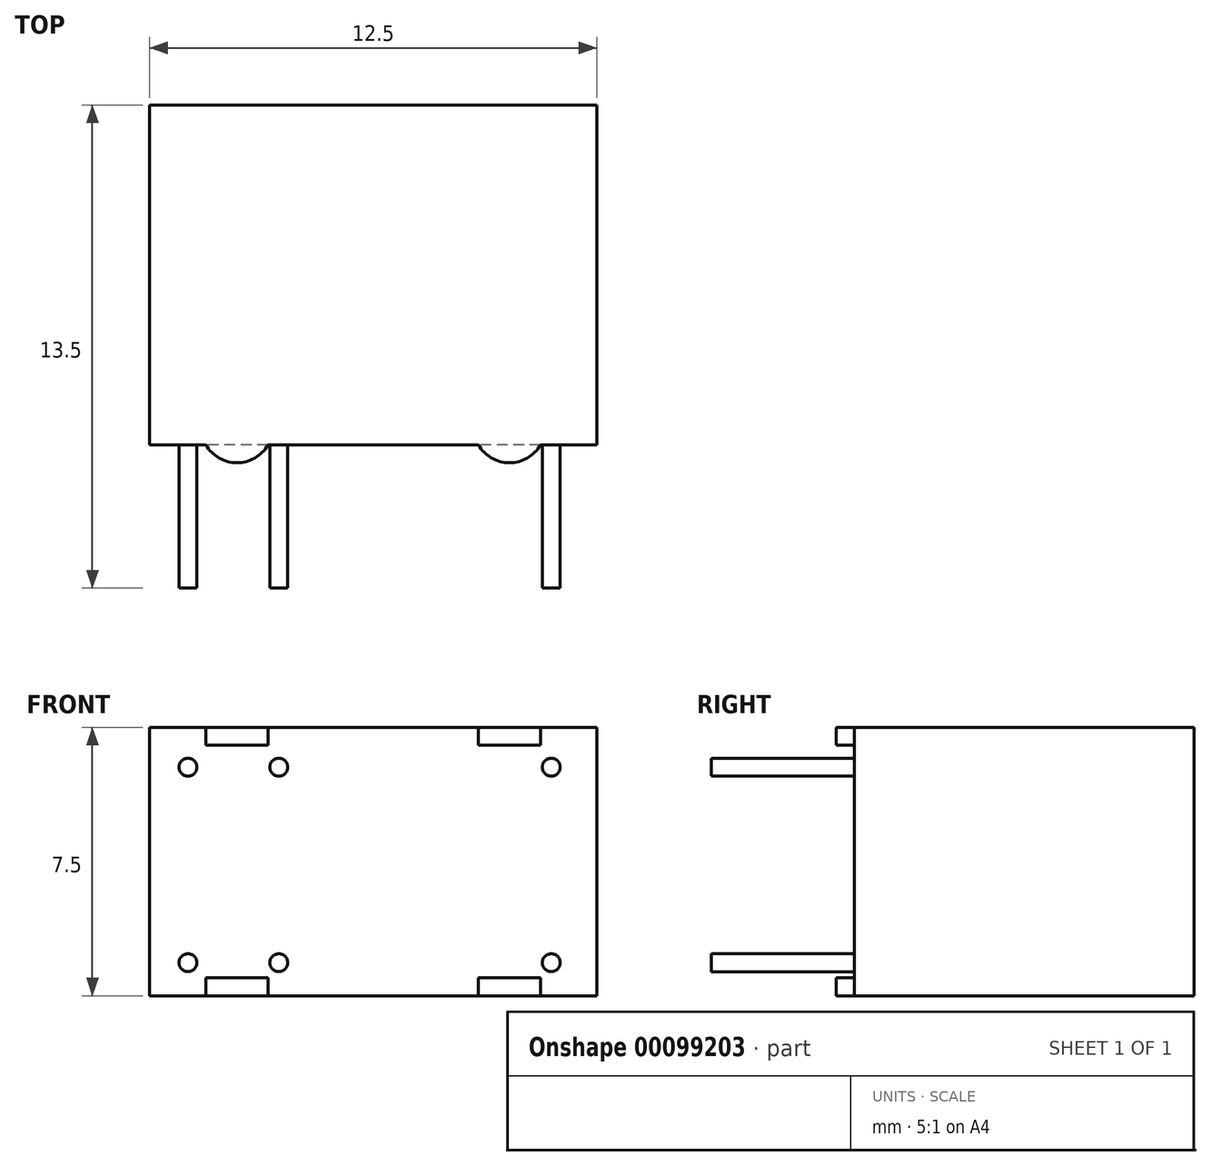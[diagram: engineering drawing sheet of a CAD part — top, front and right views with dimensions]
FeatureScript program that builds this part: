
annotation { "Feature Type Name" : "Feature", "Feature Type Description" : "" }
export const myFeature = defineFeature(function(context is Context, id is Id, definition is map)
    precondition{}
    {
        {
            var Q0;
            Q0=qCreatedBy(makeId("Top.planeOp"),FACE);
            var sketch = newSketch(context, id + "F0", { "sketchPlane" : qUnion([Q0])});
            skLineSegment(sketch, "E0.bottom", {"start": v(-6.25, 10) * mm, "end": v(6.25, 10) * mm});
            skLineSegment(sketch, "E0.top", {"start": v(-6.25, 0) * mm, "end": v(6.25, 0) * mm, "construction": true});
            skLineSegment(sketch, "E0.left", {"start": v(-6.25, 10) * mm, "end": v(-6.25, 0.5) * mm});
            skLineSegment(sketch, "E0.right", {"start": v(6.25, 10) * mm, "end": v(6.25, 0.5) * mm});
            skLineSegment(sketch, "E1", {"start": v(-6.25, 0.5) * mm, "end": v(-4.68, 0.5) * mm});
            skArc(sketch, "E2", {"start": v(-4.68, 0.5) * mm, "mid": v(-3.81, 0) * mm, "end": v(-2.94, 0.5) * mm});
            skArc(sketch, "E3", {"start": v(2.94, 0.5) * mm, "mid": v(3.81, 0) * mm, "end": v(4.68, 0.5) * mm});
            skLineSegment(sketch, "E4.trimOffspring", {"start": v(-2.94, 0.5) * mm, "end": v(2.94, 0.5) * mm});
            skLineSegment(sketch, "E5.trimOffspring", {"start": v(4.68, 0.5) * mm, "end": v(6.25, 0.5) * mm});
            skSolve(sketch);
        }
        {
            var Q0;
            Q0 = qSketchRegion(id + "F0", true);
            extrude(context, id + "F1", {"entities" : qUnion([Q0]), "depth" : (7.5 / 2) * mm, "hasSecondDirection" : true, "secondDirectionOppositeDirection" : true, "secondDirectionDepth" : (7.5 / 2) * mm});
        }
        {
            var Q0;
            Q0=makeQuery(id+"F1.opExtrude","SWEPT_FACE",FACE,{"disambiguationData":[OSD([sQuery(id+"F0.wireOp",EDGE,"E4.trimOffspring")])]});
            var sketch = newSketch(context, id + "F2", { "sketchPlane" : qUnion([Q0])});
            skLineSegment(sketch, "E6.bottom", {"start": v(6.25, -3.25) * mm, "end": v(-6.25, -3.25) * mm});
            skLineSegment(sketch, "E6.top", {"start": v(6.25, 3.25) * mm, "end": v(-6.25, 3.25) * mm});
            skLineSegment(sketch, "E6.left", {"start": v(6.25, -3.25) * mm, "end": v(6.25, 3.25) * mm});
            skLineSegment(sketch, "E6.right", {"start": v(-6.25, -3.25) * mm, "end": v(-6.25, 3.25) * mm});
            skPoint(sketch, "E6.middle", {"position": v(0, 0) * mm});
            skSolve(sketch);
        }
        {
            var Q0;
            Q0 = qSketchRegion(id + "F2", true);
            extrude(context, id + "F3", {"entities" : qUnion([Q0]), "operationType" : NewBodyOperationType.REMOVE, "endBound" : BoundingType.THROUGH_ALL, "depth" : 25 * mm});
        }
        {
            var Q0;
            Q0=makeQuery(id+"F3.boolean.opBoolean","MERGE",FACE,{"derivedFrom":[makeQuery(id+"F1.opExtrude","SWEPT_FACE",FACE,{"disambiguationData":[OSD([sQuery(id+"F0.wireOp",EDGE,"E1")])]}),makeQuery(id+"F1.opExtrude","SWEPT_FACE",FACE,{"disambiguationData":[OSD([sQuery(id+"F0.wireOp",EDGE,"E4.trimOffspring")])]}),makeQuery(id+"F1.opExtrude","SWEPT_FACE",FACE,{"disambiguationData":[OSD([sQuery(id+"F0.wireOp",EDGE,"E5.trimOffspring")])]}),makeQuery(id+"F3.opExtrude","CAP_FACE",FACE,{"disambiguationData":[OSD([sQuery(id+"F2.wireOp",EDGE,"E6.bottom"),sQuery(id+"F2.wireOp",EDGE,"E6.top"),sQuery(id+"F2.wireOp",EDGE,"E6.left"),sQuery(id+"F2.wireOp",EDGE,"E6.right")])],"isStart":true})]});
            var sketch = newSketch(context, id + "F4", { "sketchPlane" : qUnion([Q0])});
            skCircle(sketch, "E7", {"center": v(-5.18, 2.64) * mm, "radius": 0.25 * mm});
            skCircle(sketch, "E8.1.0.0", {"center": v(-2.64, 2.64) * mm, "radius": 0.25 * mm});
            skCircle(sketch, "E8.4.0.0", {"center": v(4.98, 2.64) * mm, "radius": 0.25 * mm});
            skLineSegment(sketch, "E8.direction1", {"start": v(-5.18, 2.64) * mm, "end": v(-2.64, 2.64) * mm, "construction": true});
            skCircle(sketch, "E9.1.0.0", {"center": v(4.98, -2.83) * mm, "radius": 0.25 * mm});
            skCircle(sketch, "E9.1.0.1", {"center": v(-5.18, -2.83) * mm, "radius": 0.25 * mm});
            skLineSegment(sketch, "E9.1.0.2", {"start": v(-5.18, -2.83) * mm, "end": v(-2.64, -2.83) * mm, "construction": true});
            skCircle(sketch, "E9.1.0.3", {"center": v(-2.64, -2.83) * mm, "radius": 0.25 * mm});
            skLineSegment(sketch, "E9.direction1", {"start": v(4.98, 2.64) * mm, "end": v(4.98, -2.83) * mm, "construction": true});
            skSolve(sketch);
        }
        {
            var Q0;
            Q0 = qSketchRegion(id + "F4", true);
            extrude(context, id + "F5", {"entities" : qUnion([Q0]), "operationType" : NewBodyOperationType.ADD, "depth" : 4 * mm});
        }
    });
